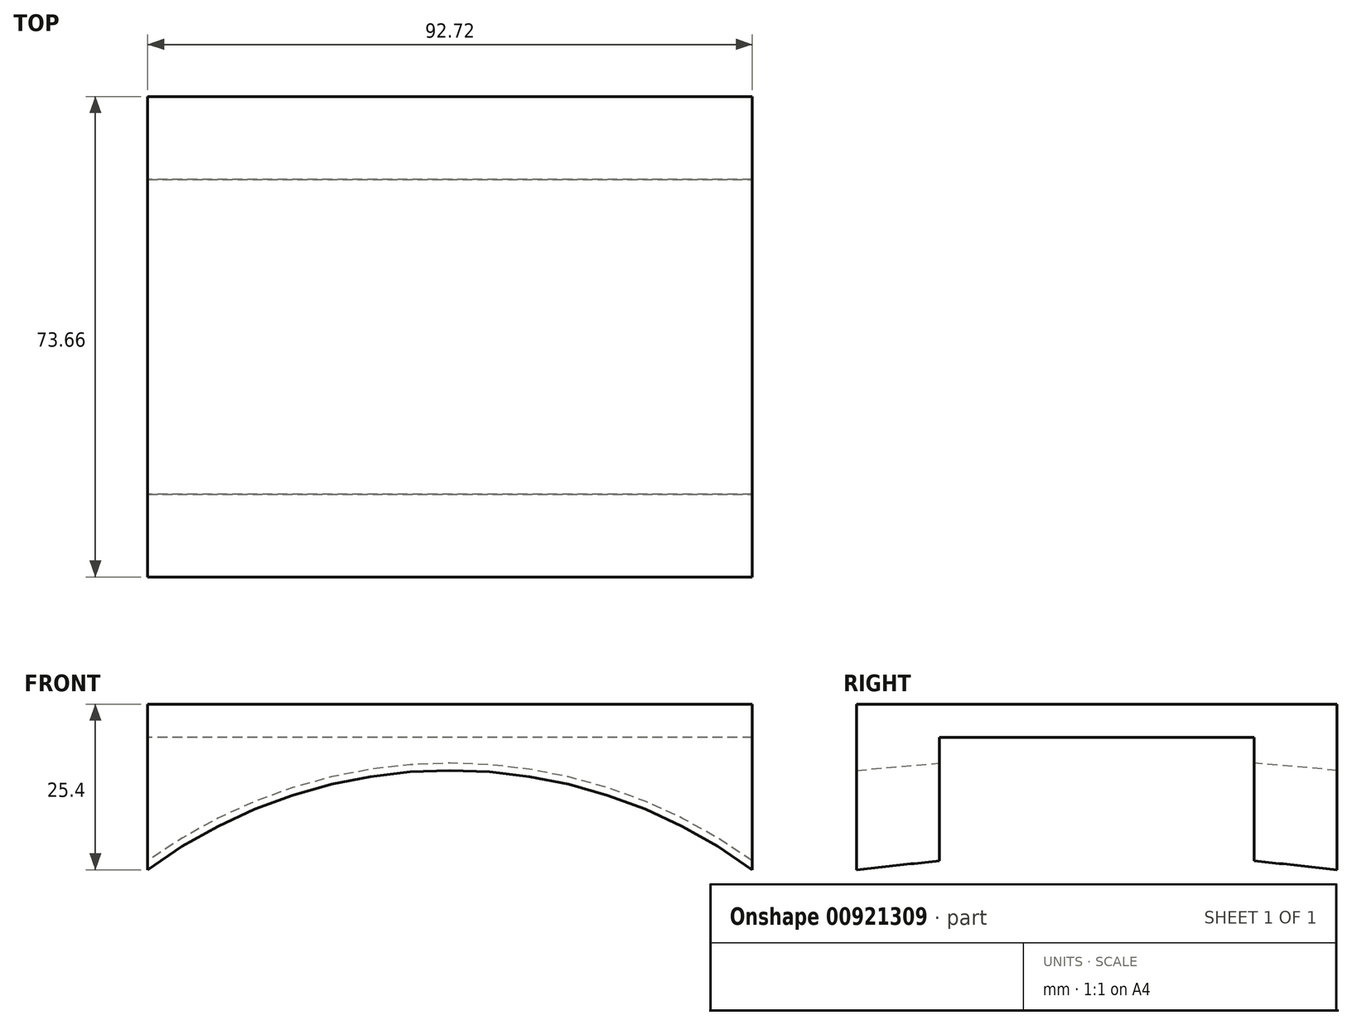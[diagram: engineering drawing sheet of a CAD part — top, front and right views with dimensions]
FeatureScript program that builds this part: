
annotation { "Feature Type Name" : "Feature", "Feature Type Description" : "" }
export const myFeature = defineFeature(function(context is Context, id is Id, definition is map)
    precondition{}
    {
        {
            var Q0;
            Q0=qCreatedBy(makeId("Top.planeOp"),FACE);
            var sketch = newSketch(context, id + "F0", { "sketchPlane" : qUnion([Q0])});
            skLineSegment(sketch, "E0.bottom", {"start": v(-46.35, 36.83) * mm, "end": v(46.35, 36.83) * mm});
            skLineSegment(sketch, "E0.top", {"start": v(-46.35, -36.83) * mm, "end": v(46.35, -36.83) * mm});
            skLineSegment(sketch, "E0.left", {"start": v(-46.35, 36.83) * mm, "end": v(-46.35, -36.83) * mm});
            skLineSegment(sketch, "E0.right", {"start": v(46.35, 36.83) * mm, "end": v(46.35, -36.83) * mm});
            skSolve(sketch);
        }
        {
            var Q0;
            Q0=makeQuery(id+"F0.imprint","IMPRINT",FACE,{"disambiguationData":[TD([[makeQuery(id+"F0.imprint","IMPRINT",EDGE,{"derivedFrom":sQuery(id+"F0.wireOp",EDGE,"E0.bottom")}),-1.0]])]});
            extrude(context, id + "F1", {"entities" : qUnion([Q0]), "depth" : 5.08 * mm, "offsetDistance" : 25.4 * mm});
        }
        {
            var Q0;
            Q0=makeQuery(id+"F1.opExtrude","CAP_FACE",FACE,{"disambiguationData":[OSD([sQuery(id+"F0.wireOp",EDGE,"E0.bottom"),sQuery(id+"F0.wireOp",EDGE,"E0.top"),sQuery(id+"F0.wireOp",EDGE,"E0.left"),sQuery(id+"F0.wireOp",EDGE,"E0.right")])],"isStart":true});
            var sketch = newSketch(context, id + "F2", { "sketchPlane" : qUnion([Q0])});
            skLineSegment(sketch, "E1.bottom", {"start": v(-46.35, -36.83) * mm, "end": v(46.35, -36.83) * mm});
            skLineSegment(sketch, "E1.top", {"start": v(-46.35, -24.13) * mm, "end": v(46.35, -24.13) * mm});
            skLineSegment(sketch, "E1.left", {"start": v(-46.35, -36.83) * mm, "end": v(-46.35, -24.13) * mm});
            skLineSegment(sketch, "E1.right", {"start": v(46.35, -36.83) * mm, "end": v(46.35, -24.13) * mm});
            skLineSegment(sketch, "E2.bottom", {"start": v(46.35, 36.83) * mm, "end": v(-46.35, 36.83) * mm});
            skLineSegment(sketch, "E2.top", {"start": v(46.36, 24.13) * mm, "end": v(-46.35, 24.13) * mm});
            skLineSegment(sketch, "E2.left", {"start": v(46.35, 36.83) * mm, "end": v(46.35, 24.13) * mm});
            skLineSegment(sketch, "E2.right", {"start": v(-46.35, 36.83) * mm, "end": v(-46.35, 24.13) * mm});
            skSolve(sketch);
        }
        {
            var Q0;
            Q0=makeQuery(id+"F2.imprint","IMPRINT",FACE,{"disambiguationData":[TD([[makeQuery(id+"F2.imprint","IMPRINT",EDGE,{"derivedFrom":sQuery(id+"F2.wireOp",EDGE,"E2.bottom")}),-1.0]])]});
            var Q1;
            Q1=makeQuery(id+"F2.imprint","IMPRINT",FACE,{"disambiguationData":[TD([[makeQuery(id+"F2.imprint","IMPRINT",EDGE,{"derivedFrom":sQuery(id+"F2.wireOp",EDGE,"E1.bottom")}),1.0]])]});
            extrude(context, id + "F3", {"entities" : qUnion([Q0, Q1]), "operationType" : NewBodyOperationType.ADD, "flatOperationType" : FlatOperationType.REMOVE, "depth" : 20.32 * mm, "offsetDistance" : 25.4 * mm, "domain" : OperationDomain.MODEL});
        }
        {
            var Q0;
            Q0=makeQuery(id+"F3.boolean.opBoolean","MERGE",FACE,{"derivedFrom":[makeQuery(id+"F1.opExtrude","SWEPT_FACE",FACE,{"disambiguationData":[OSD([sQuery(id+"F0.wireOp",EDGE,"E0.top")])]}),makeQuery(id+"F3.opExtrude","SWEPT_FACE",FACE,{"disambiguationData":[OSD([sQuery(id+"F2.wireOp",EDGE,"E2.bottom")])]})]});
            var sketch = newSketch(context, id + "F4", { "sketchPlane" : qUnion([Q0])});
            skArc(sketch, "E3", {"start": v(46.35, -20.32) * mm, "mid": v(0, -5.08) * mm, "end": v(-46.35, -20.32) * mm});
            skLineSegment(sketch, "E4", {"start": v(-46.35, -20.32) * mm, "end": v(46.35, -20.32) * mm});
            skSolve(sketch);
        }
        {
            var Q0;
            Q0=makeQuery(id+"F4.imprint","IMPRINT",FACE,{"disambiguationData":[TD([[makeQuery(id+"F4.imprint","IMPRINT",EDGE,{"derivedFrom":sQuery(id+"F4.wireOp",EDGE,"E3")}),1.0]])]});
            extrude(context, id + "F5", {"entities" : qUnion([Q0]), "operationType" : NewBodyOperationType.REMOVE, "endBound" : BoundingType.THROUGH_ALL, "oppositeDirection" : true, "depth" : 25.4 * mm, "offsetDistance" : 25.4 * mm});
        }
        {
            var Q0;
            Q0=makeQuery(id+"F5.boolean.opBoolean","INTERSECT",EDGE,{"derivedFrom":[makeQuery(id+"F3.opExtrude","SWEPT_FACE",FACE,{"disambiguationData":[OSD([sQuery(id+"F2.wireOp",EDGE,"E2.top")])]}),makeQuery(id+"F5.opExtrude","SWEPT_FACE",FACE,{"disambiguationData":[OSD([sQuery(id+"F4.wireOp",EDGE,"E3")])]})]});
            var Q1;
            Q1=makeQuery(id+"F5.boolean.opBoolean","INTERSECT",EDGE,{"derivedFrom":[makeQuery(id+"F3.opExtrude","SWEPT_FACE",FACE,{"disambiguationData":[OSD([sQuery(id+"F2.wireOp",EDGE,"E1.top")])]}),makeQuery(id+"F5.opExtrude","SWEPT_FACE",FACE,{"disambiguationData":[OSD([sQuery(id+"F4.wireOp",EDGE,"E3")])]})]});
            chamfer(context, id + "F6", {"entities" : qUnion([Q0, Q1]), "chamferType" : ChamferType.OFFSET_ANGLE, "width" : 12.7 * mm, "oppositeDirection" : false, "angle" : 5 * degree, "tangentPropagation" : true});
        }
    });
